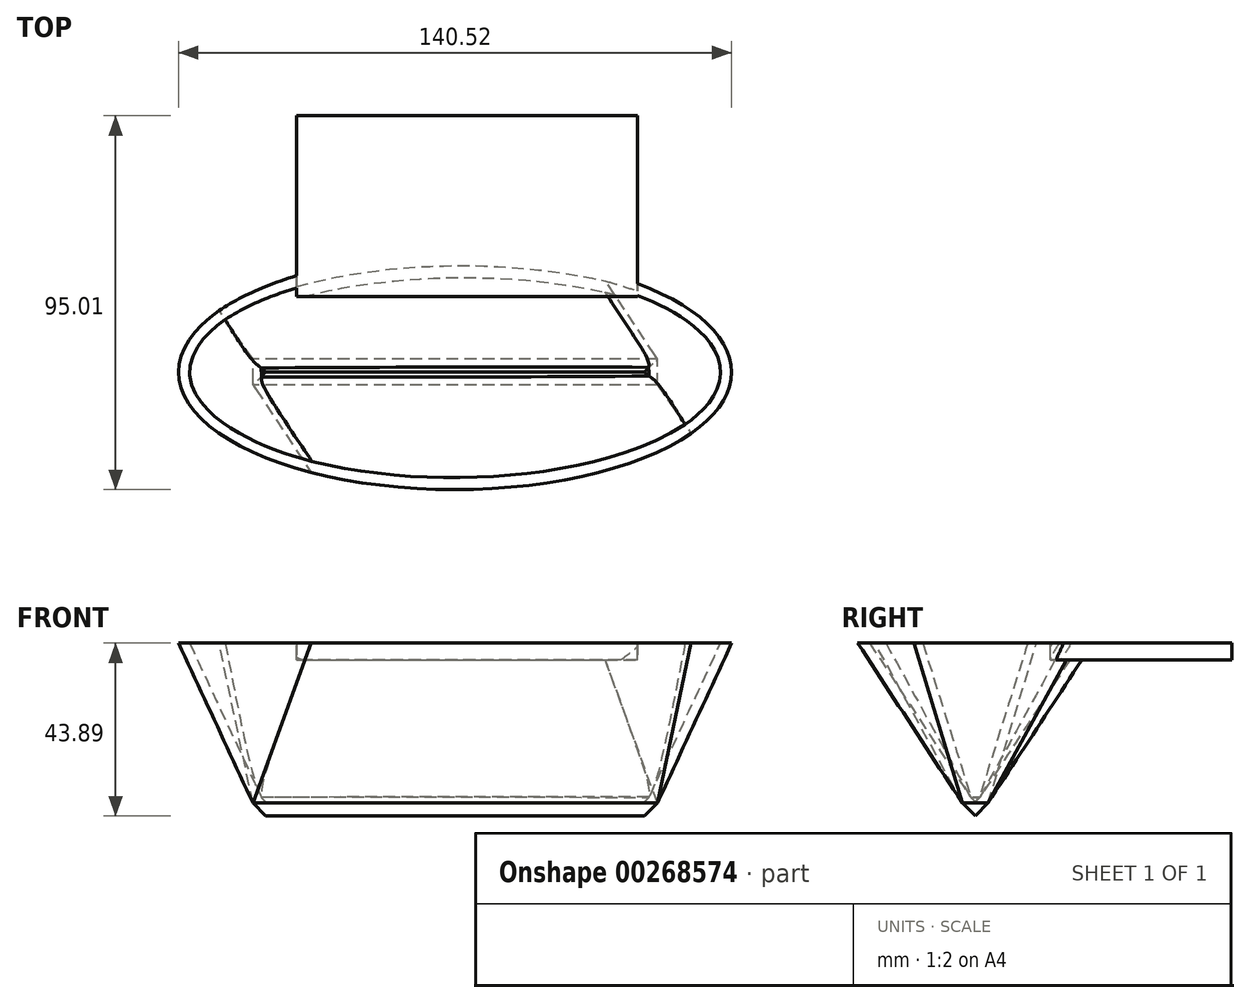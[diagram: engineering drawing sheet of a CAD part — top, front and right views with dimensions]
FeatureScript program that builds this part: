
annotation { "Feature Type Name" : "Feature", "Feature Type Description" : "" }
export const myFeature = defineFeature(function(context is Context, id is Id, definition is map)
    precondition{}
    {
        {
            var Q0;
            Q0=qCreatedBy(makeId("Top.planeOp"),FACE);
            var sketch = newSketch(context, id + "F0", { "sketchPlane" : qUnion([Q0])});
            skEllipse(sketch, "E0", {"center": v(0, 0) * mm, "majorRadius": 70.26 * mm, "minorRadius": 29.87 * mm, "majorAxis": v(1, 0)});
            skSolve(sketch);
        }
        {
            var Q0;
            Q0=qCreatedBy(makeId("Top.planeOp"),FACE);
            cPlane(context, id + "F1", {"entities" : qUnion([Q0]), "cplaneType" : CPlaneType.OFFSET, "offset" : 40.64 * mm, "oppositeDirection" : true, "width" : 152.4 * mm, "height" : 152.4 * mm});
        }
        {
            var Q0;
            Q0=qCreatedBy(id+"F1.planeOp",FACE);
            var sketch = newSketch(context, id + "F2", { "sketchPlane" : qUnion([Q0])});
            skLineSegment(sketch, "E1.bottom", {"start": v(51.38, -3.25) * mm, "end": v(-51.38, -3.25) * mm});
            skLineSegment(sketch, "E1.top", {"start": v(51.38, 3.25) * mm, "end": v(-51.38, 3.25) * mm});
            skLineSegment(sketch, "E1.left", {"start": v(51.38, -3.25) * mm, "end": v(51.38, 3.25) * mm});
            skLineSegment(sketch, "E1.right", {"start": v(-51.38, -3.25) * mm, "end": v(-51.38, 3.25) * mm});
            skPoint(sketch, "E1.middle", {"position": v(0, 0) * mm});
            skSolve(sketch);
        }
        {
            var Q0;
            Q0=makeQuery(id+"F2.imprint","IMPRINT",FACE,{"disambiguationData":[TD([[makeQuery(id+"F2.imprint","IMPRINT",EDGE,{"derivedFrom":sQuery(id+"F2.wireOp",EDGE,"E1.bottom")}),-1.0]])]});
            var Q1;
            Q1=makeQuery(id+"F0.imprint","IMPRINT",FACE,{"disambiguationData":[TD([[makeQuery(id+"F0.imprint","IMPRINT",EDGE,{"derivedFrom":sQuery(id+"F0.wireOp",EDGE,"E0")}),1.0]])]});
            loft(context, id + "F3", {"sheetProfilesArray" : [{ "sheetProfileEntities" : qUnion([Q0]) }, { "sheetProfileEntities" : qUnion([Q1]) }]});
        }
        {
            var Q0;
            Q0=makeQuery(id+"F3.opLoft","CAP_FACE",FACE,{"disambiguationData":[OSD([makeQuery(id+"F2.imprint","IMPRINT",FACE,{"disambiguationData":[TD([[makeQuery(id+"F2.imprint","IMPRINT",EDGE,{"derivedFrom":sQuery(id+"F2.wireOp",EDGE,"E1.bottom")}),-1.0]])]})])],"isStart":true});
            extrude(context, id + "F4", {"entities" : qUnion([Q0]), "operationType" : NewBodyOperationType.ADD, "depth" : 25.4 * mm, "hasDraft" : true, "draftAngle" : 45 * degree, "draftPullDirection" : true});
        }
        {
            var Q0;
            Q0=makeQuery(id+"F3.opLoft","CAP_FACE",FACE,{"disambiguationData":[OSD([makeQuery(id+"F0.imprint","IMPRINT",FACE,{"disambiguationData":[TD([[makeQuery(id+"F0.imprint","IMPRINT",EDGE,{"derivedFrom":sQuery(id+"F0.wireOp",EDGE,"E0")}),1.0]])]})])],"isStart":true});
            shell(context, id + "F5", {"entities" : qUnion([Q0]), "thickness" : 2.54 * mm});
        }
        {
            var Q0;
            Q0=qCreatedBy(makeId("Top.planeOp"),FACE);
            var sketch = newSketch(context, id + "F6", { "sketchPlane" : qUnion([Q0])});
            skLineSegment(sketch, "E2.bottom", {"start": v(46.38, 19.13) * mm, "end": v(-40.32, 19.13) * mm});
            skLineSegment(sketch, "E2.top", {"start": v(46.38, 65.14) * mm, "end": v(-40.32, 65.14) * mm});
            skLineSegment(sketch, "E2.left", {"start": v(46.38, 19.13) * mm, "end": v(46.38, 65.14) * mm});
            skLineSegment(sketch, "E2.right", {"start": v(-40.32, 19.13) * mm, "end": v(-40.32, 65.14) * mm});
            skSolve(sketch);
        }
        {
            var Q0;
            Q0 = qSketchRegion(id + "F6", true);
            extrude(context, id + "F7", {"entities" : qUnion([Q0]), "operationType" : NewBodyOperationType.ADD, "oppositeDirection" : true, "depth" : 4.32 * mm});
        }
    });
